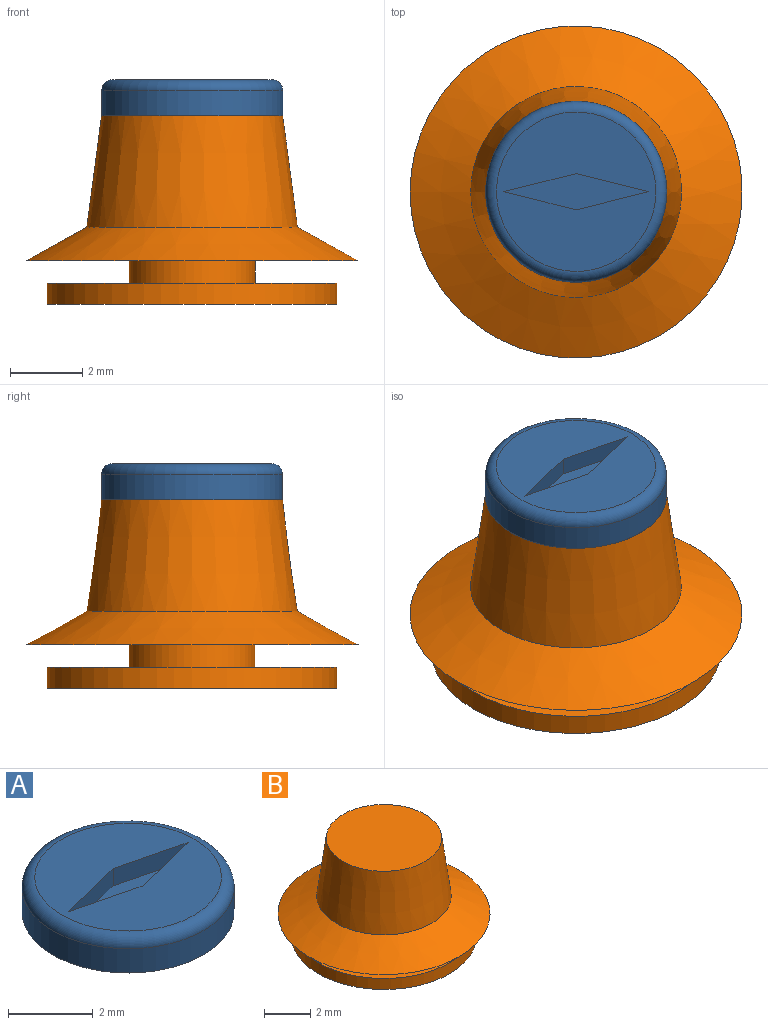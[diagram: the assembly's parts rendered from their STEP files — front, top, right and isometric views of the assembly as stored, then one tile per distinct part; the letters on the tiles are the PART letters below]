
ASSEMBLY  parts=2 mates=1
PART A: 9 faces, bbox 5.4x5.4x1 mm
  f0: plane 4.4x4.4mm, normal (0,0,1), area 13.2mm2, adj f3,f4,f5,f6,f7
  f1: plane 5x5mm, normal (0,0,-1), area 19.6mm2, adj f2
  f2: cylinder r=2.5mm len=5mm, axis (0,0,1), area 11mm2, adj f1,f3
  f3: torus R=2.2mm, axis (0,0,1), area 7.1mm2, adj f0,f2
  f4: plane 2x0.5mm, normal (0.24,-0.97,0), area 1mm2, adj f0,f5,f7,f8
  f5: plane 2x0.5mm, normal (0.24,0.97,0), area 1mm2, adj f0,f4,f6,f8
  f6: plane 2x0.5mm, normal (-0.24,0.97,0), area 1mm2, adj f0,f5,f7,f8
  f7: plane 2x0.5mm, normal (-0.24,-0.97,0), area 1mm2, adj f0,f4,f6,f8
  f8: plane 4x1mm, normal (0,0,1), area 2mm2, adj f4,f5,f6,f7
PART B: 8 faces, bbox 9.2x9.2x5.2 mm
  f0: plane 8x8mm, normal (0,0,-1), area 50.3mm2, adj f1
  f1: cylinder r=4mm len=8mm, axis (0,0,-1), area 14.6mm2, adj f0,f2
  f2: plane 8x8mm, normal (0,0,1), area 40.8mm2, adj f1,f3
  f3: cylinder r=1.74mm len=3.48mm, axis (0,0,-1), area 6.8mm2, adj f2,f4
  f4: plane 9.17x9.17mm, normal (0,0,-1), area 56.5mm2, adj f3,f5
  f5: cone r=2.91mm half-angle=61deg, axis (0,0,-1), area 45.1mm2, adj f4,f6
  f6: cone r=2.5mm half-angle=7.6deg, axis (0,0,-1), area 52.7mm2, adj f5,f7
  f7: plane 5x5mm, normal (0,0,1), area 19.6mm2, adj f6
PLACE A t=(0,0,5)mm
PLACE B at identity fixed
MATE fastened A.f2 <-> B.f1  axis (0,0,-1) through (0,0,4)mm
